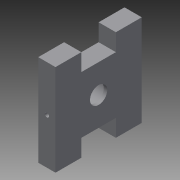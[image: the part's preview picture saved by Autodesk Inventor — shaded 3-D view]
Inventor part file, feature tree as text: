
AUTODESK INVENTOR PART (.ipt)
format: ipt  version: 2015 (Build 190159000, 159)  size: 118,272 bytes
history: native  units: mm
features: sketch x6, extrude x4, fillet x1
ambient origin geometry x8: Origin, YZ Plane, XZ Plane, XY Plane, X Axis, Y Axis, Z Axis, Center Point
bodies: Solid1 (feature_tree)
feature tree (11):
  sketch  "Sketch1"  dims[d0=50.0mm d1=53.0mm]
  sketch  "Sketch2"  dims[d2=15.0mm d3=10.0mm]
  extrude  "Extrusion1"  Depth=53.0mm
  sketch  "Sketch4"  dims[d6=15.0mm d7=10.0mm d8=20.0mm]
  sketch  "Sketch5"  dims[d9=10.0mm]
  sketch  "Sketch6"  dims[d10=15.0mm d11=10.0mm d12=0.0mm d13=15.0mm d28=10.0mm d29=0.0mm d30=2.5mm d31=10.0mm d32=0.0mm d33=10.0mm d34=2.0mm d35=0.0mm d36=2.0mm]
  extrude  "Extrusion2"  Depth=10.0mm
  extrude  "Extrusion3"  Depth=10.0mm
  extrude  "Extrusion4"  Depth=10.0mm
  fillet  "Fillet1"  Radius=20.0mm
  sketch  "Sketch3"  dims[d4=20.0mm d5=10.0mm]
